# Revit family: Rectangular acrylic one-piece bath with integrated panel and waste kit-Element-248158xx1
name_source: partatom
category: Plumbing Fixtures
revit_build: Autodesk Revit Architecture 2014 (Build: 20130308_1515(x64)
units: mm (PartAtom-declared; Revit-internal decimal feet)

## types (1)
- 248158001 White
    Description = Rectangular acrylic one-piece bath with integrated panel and waste kit
    Drain Diameter = 52 mm
    Drain included = Yes
    Height = 580 mm  [stored 1.90289 ft]
    Inside height (mm) = 445 mm  [stored 1.45997 ft]
    Inside length (mm) = 1672 mm  [stored 5.48556 ft]
    Installation structure = Naked
    Installation type = Freestanding
    Length = 1800 mm  [stored 5.90551 ft]
    Manufacturer URL = www.roca.com
    Material = Acrylic
    Model = 248158..1
    People capacity = 1
    Primary Material = White - Element - Roca
    Product data url = http://bimobject.com
    Secondary Material = Chrome-Element-Roca
    Shape = Rectangular
    Sound insulation = Yes
    URL = http://www.export.roca.com
    Water capacity (L) = 280
    Width = 800 mm  [stored 2.62467 ft]

note: [stored X ft] marks values corroborated as IEEE doubles in the binary element streams (Revit-internal decimal feet)

## geometry (parser evidence)
native form markers: Extrusion x1, Sweep x1
no freeform markers — native parametric forms only
